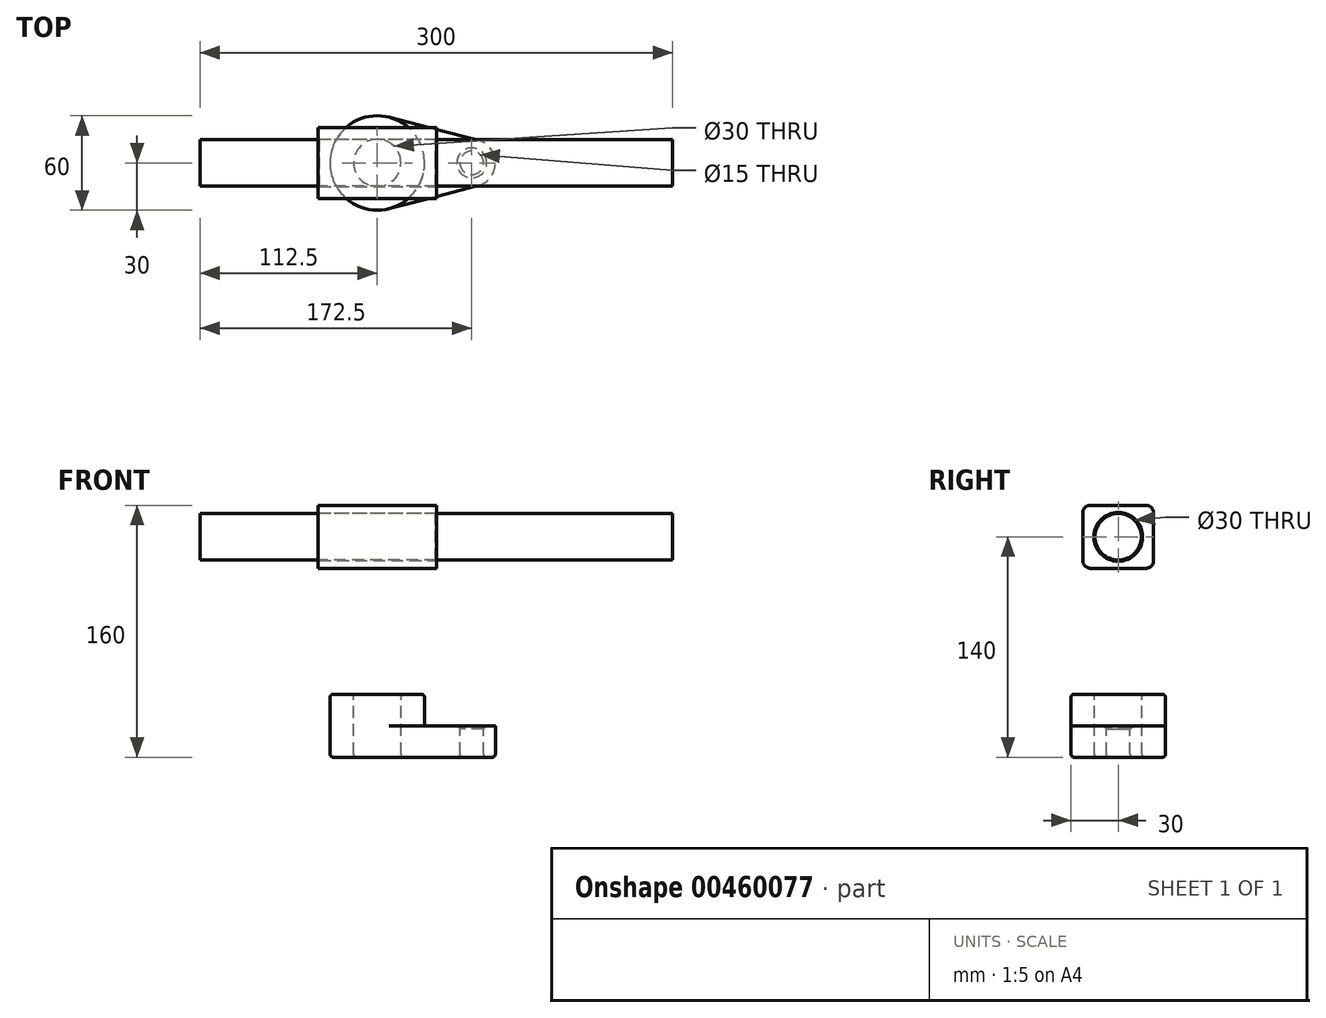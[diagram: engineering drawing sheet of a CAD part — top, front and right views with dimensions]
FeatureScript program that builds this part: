
annotation { "Feature Type Name" : "Feature", "Feature Type Description" : "" }
export const myFeature = defineFeature(function(context is Context, id is Id, definition is map)
    precondition{}
    {
        {
            var Q0;
            Q0=qCreatedBy(makeId("Top.planeOp"),FACE);
            var sketch = newSketch(context, id + "F0", { "sketchPlane" : qUnion([Q0])});
            skCircle(sketch, "E0", {"center": v(0, 0) * mm, "radius": 30 * mm});
            skCircle(sketch, "E1", {"center": v(60, 0) * mm, "radius": 15 * mm});
            skLineSegment(sketch, "E2", {"start": v(7.5, 29.05) * mm, "end": v(63.75, 14.52) * mm});
            skLineSegment(sketch, "E3", {"start": v(7.5, -29.05) * mm, "end": v(63.75, -14.52) * mm});
            skCircle(sketch, "E4", {"center": v(0, 0) * mm, "radius": 15 * mm});
            skCircle(sketch, "E5", {"center": v(60, 0) * mm, "radius": 7.5 * mm});
            skSolve(sketch);
        }
        {
            var Q0;
            Q0=makeQuery(id+"F0.imprint","IMPRINT",FACE,{"disambiguationData":[TD([[makeQuery(id+"F0.imprint","IMPRINT",EDGE,{"derivedFrom":sQuery(id+"F0.wireOp",EDGE,"E4")}),-1.0]])]});
            var Q1;
            {var subQ0=sQuery(id+"F0.wireOp",EDGE,"E2");Q1=makeQuery(id+"F0.imprint","IMPRINT",FACE,{"disambiguationData":[TD([[makeQuery(id+"F0.imprint","IMPRINT",EDGE,{"derivedFrom":subQ0}),-1.0]])]});}
            var Q2;
            Q2=makeQuery(id+"F0.imprint","IMPRINT",FACE,{"disambiguationData":[TD([[makeQuery(id+"F0.imprint","IMPRINT",EDGE,{"derivedFrom":sQuery(id+"F0.wireOp",EDGE,"E5")}),-1.0]])]});
            extrude(context, id + "F1", {"entities" : qUnion([Q0, Q1, Q2]), "oppositeDirection" : true, "depth" : 20 * mm});
        }
        {
            var Q0;
            Q0=makeQuery(id+"F0.imprint","IMPRINT",FACE,{"disambiguationData":[TD([[makeQuery(id+"F0.imprint","IMPRINT",EDGE,{"derivedFrom":sQuery(id+"F0.wireOp",EDGE,"E4")}),-1.0]])]});
            extrude(context, id + "F2", {"entities" : qUnion([Q0]), "operationType" : NewBodyOperationType.ADD, "depth" : 20 * mm});
        }
        {
            var Q0;
            Q0=makeQuery(id+"F2.opExtrude","CAP_EDGE",EDGE,{"disambiguationData":[OSD([sQuery(id+"F0.wireOp",EDGE,"E0")])],"isStart":false});
            var Q1;
            Q1=makeQuery(id+"F2.opExtrude","CAP_EDGE",EDGE,{"disambiguationData":[OSD([sQuery(id+"F0.wireOp",EDGE,"E4")])],"isStart":false});
            var Q2;
            Q2=makeQuery(id+"F1.opExtrude","CAP_FACE",FACE,{"disambiguationData":[OSD([sQuery(id+"F0.wireOp",EDGE,"E0"),sQuery(id+"F0.wireOp",EDGE,"E1"),sQuery(id+"F0.wireOp",EDGE,"E2"),sQuery(id+"F0.wireOp",EDGE,"E3"),sQuery(id+"F0.wireOp",EDGE,"E4"),sQuery(id+"F0.wireOp",EDGE,"E5")])],"isStart":false});
            fillet(context, id + "F3", {"entities" : qUnion([Q0, Q1, Q2]), "radius" : 2 * mm, "tangentPropagation" : true, "allowEdgeOverflow" : false});
        }
        {
            var Q0;
            Q0=makeQuery(id+"F1.opExtrude","CAP_EDGE",EDGE,{"disambiguationData":[OSD([sQuery(id+"F0.wireOp",EDGE,"E5")])],"isStart":true});
            chamfer(context, id + "F4", {"entities" : qUnion([Q0]), "width" : 2 * mm, "tangentPropagation" : true});
        }
        {
            var Q0;
            Q0=qCreatedBy(makeId("Right.planeOp"),FACE);
            var sketch = newSketch(context, id + "F5", { "sketchPlane" : qUnion([Q0])});
            skCircle(sketch, "E6", {"center": v(0, 120) * mm, "radius": 15 * mm});
            skLineSegment(sketch, "E7", {"start": v(22.5, 140) * mm, "end": v(22.5, 100) * mm});
            skLineSegment(sketch, "E8", {"start": v(22.5, 100) * mm, "end": v(-22.5, 100) * mm});
            skLineSegment(sketch, "E9", {"start": v(-22.5, 100) * mm, "end": v(-22.5, 140) * mm});
            skLineSegment(sketch, "E10", {"start": v(22.5, 140) * mm, "end": v(-22.5, 140) * mm});
            skSolve(sketch);
        }
        {
            var Q0;
            Q0 = qSketchRegion(id + "F5", true);
            extrude(context, id + "F6", {"entities" : qUnion([Q0]), "endBound" : BoundingType.SYMMETRIC, "oppositeDirection" : true, "depth" : 75 * mm});
        }
        {
            var Q0;
            Q0=makeQuery(id+"F6.opExtrude","CAP_EDGE",EDGE,{"disambiguationData":[OSD([sQuery(id+"F5.wireOp",EDGE,"E6")])],"isStart":true});
            var Q1;
            Q1=makeQuery(id+"F6.opExtrude","CAP_EDGE",EDGE,{"disambiguationData":[OSD([sQuery(id+"F5.wireOp",EDGE,"E6")])],"isStart":false});
            chamfer(context, id + "F7", {"entities" : qUnion([Q0, Q1]), "width" : .5 * mm, "tangentPropagation" : true});
        }
        {
            var Q0;
            Q0=makeQuery(id+"F6.opExtrude","SWEPT_EDGE",EDGE,{"disambiguationData":[OSD([sQuery(id+"F5.wireOp",EDGE,"E7"),sQuery(id+"F5.wireOp",EDGE,"E10")])]});
            var Q1;
            Q1=makeQuery(id+"F6.opExtrude","SWEPT_EDGE",EDGE,{"disambiguationData":[OSD([sQuery(id+"F5.wireOp",EDGE,"E9"),sQuery(id+"F5.wireOp",EDGE,"E10")])]});
            var Q2;
            Q2=makeQuery(id+"F6.opExtrude","SWEPT_EDGE",EDGE,{"disambiguationData":[OSD([sQuery(id+"F5.wireOp",EDGE,"E7"),sQuery(id+"F5.wireOp",EDGE,"E8")])]});
            var Q3;
            Q3=makeQuery(id+"F6.opExtrude","SWEPT_EDGE",EDGE,{"disambiguationData":[OSD([sQuery(id+"F5.wireOp",EDGE,"E8"),sQuery(id+"F5.wireOp",EDGE,"E9")])]});
            fillet(context, id + "F8", {"entities" : qUnion([Q0, Q1, Q2, Q3]), "radius" : 5 * mm, "tangentPropagation" : true, "allowEdgeOverflow" : false});
        }
        {
            var Q0;
            Q0=makeQuery(id+"F6.opExtrude","CAP_FACE",FACE,{"disambiguationData":[OSD([sQuery(id+"F5.wireOp",EDGE,"E6"),sQuery(id+"F5.wireOp",EDGE,"E7"),sQuery(id+"F5.wireOp",EDGE,"E8"),sQuery(id+"F5.wireOp",EDGE,"E9"),sQuery(id+"F5.wireOp",EDGE,"E10")])],"isStart":true});
            var sketch = newSketch(context, id + "F9", { "sketchPlane" : qUnion([Q0])});
            skCircle(sketch, "E11", {"center": v(0, 120) * mm, "radius": 14.75 * mm});
            skSolve(sketch);
        }
        {
            var Q0;
            Q0=makeQuery(id+"F9.imprint","IMPRINT",FACE,{"disambiguationData":[TD([[makeQuery(id+"F9.imprint","IMPRINT",EDGE,{"derivedFrom":sQuery(id+"F9.wireOp",EDGE,"E11")}),1.0]])]});
            extrude(context, id + "F10", {"entities" : qUnion([Q0]), "endBound" : BoundingType.SYMMETRIC, "depth" : 300 * mm});
        }
    });
